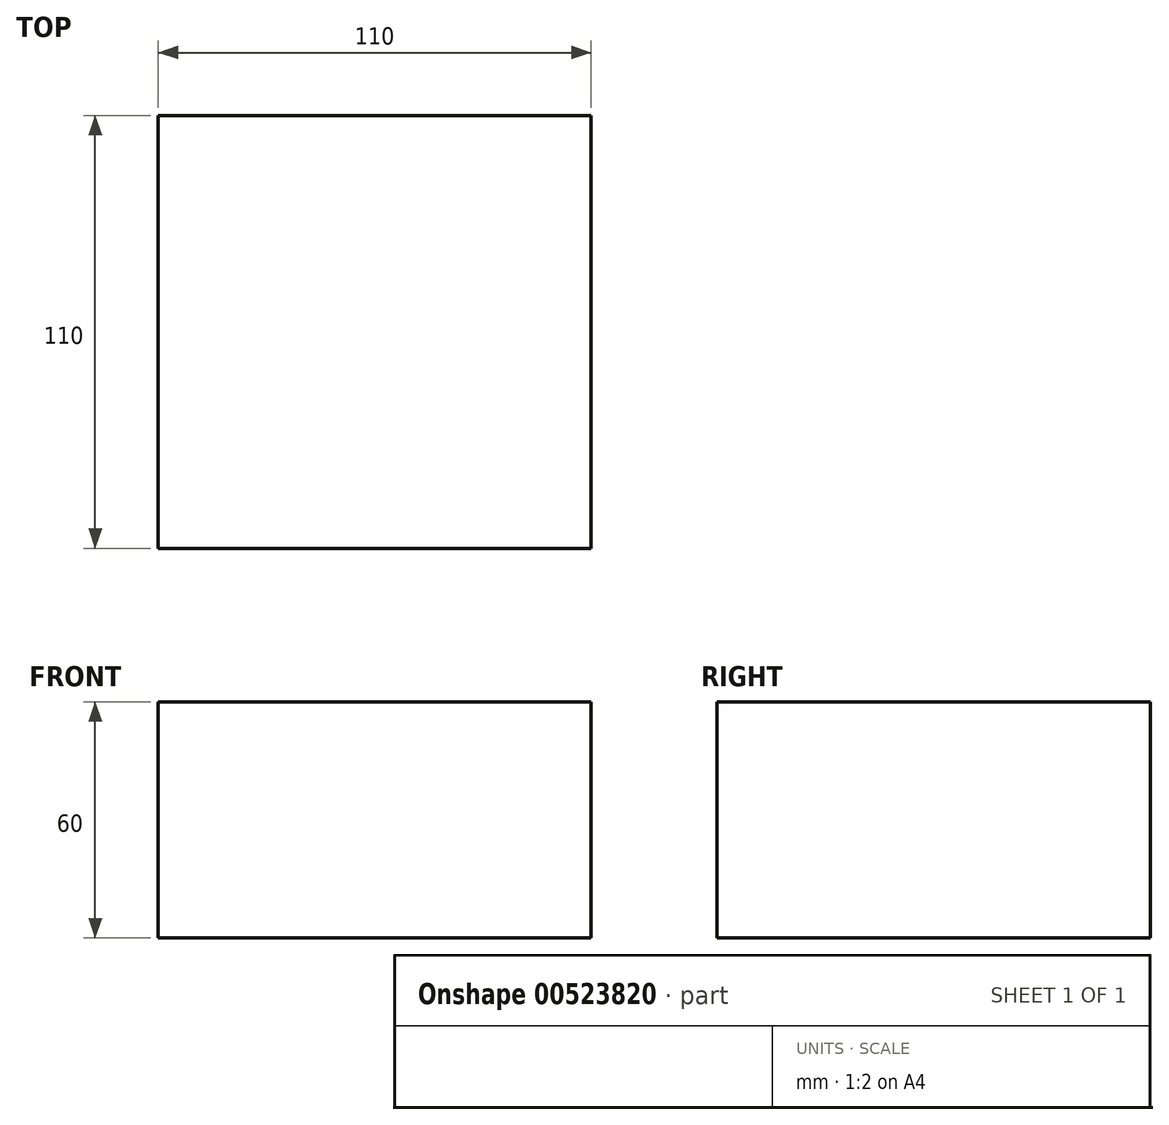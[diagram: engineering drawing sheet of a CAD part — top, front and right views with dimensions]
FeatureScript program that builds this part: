
annotation { "Feature Type Name" : "Feature", "Feature Type Description" : "" }
export const myFeature = defineFeature(function(context is Context, id is Id, definition is map)
    precondition{}
    {
        {
            var Q0;
            Q0=qCreatedBy(makeId("Top.planeOp"),FACE);
            var sketch = newSketch(context, id + "F0", { "sketchPlane" : qUnion([Q0])});
            skLineSegment(sketch, "E0.bottom", {"start": v(0, 0) * mm, "end": v(110, 0) * mm});
            skLineSegment(sketch, "E0.top", {"start": v(0, 110) * mm, "end": v(110, 110) * mm});
            skLineSegment(sketch, "E0.left", {"start": v(0, 0) * mm, "end": v(0, 110) * mm});
            skLineSegment(sketch, "E0.right", {"start": v(110, 0) * mm, "end": v(110, 110) * mm});
            skSolve(sketch);
        }
        {
            var Q0;
            Q0 = qSketchRegion(id + "F0", true);
            extrude(context, id + "F1", {"entities" : qUnion([Q0]), "depth" : 60 * mm, "offsetDistance" : 25 * mm});
        }
    });
